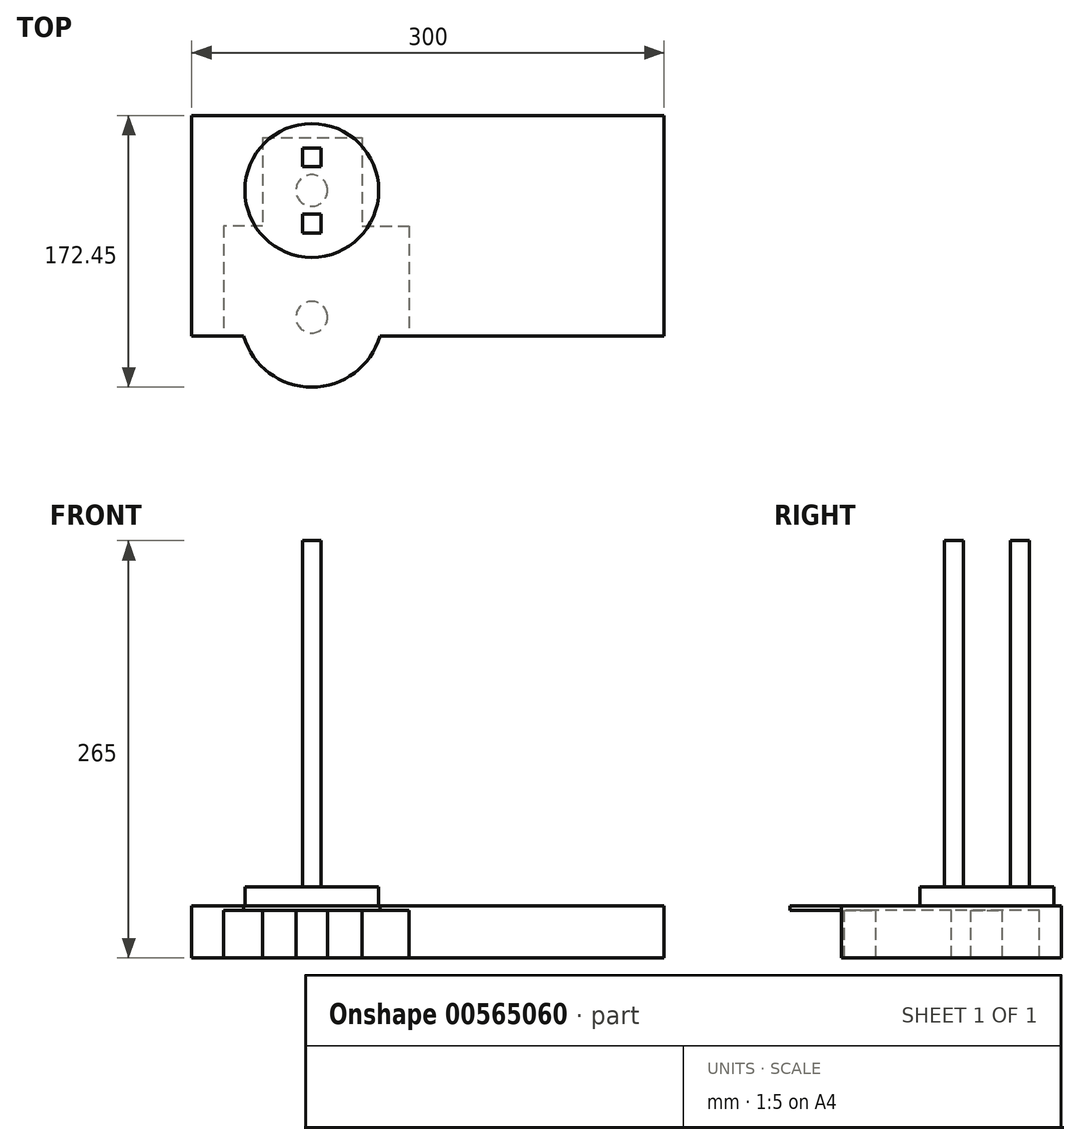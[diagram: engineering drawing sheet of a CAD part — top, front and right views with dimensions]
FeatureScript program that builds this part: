
annotation { "Feature Type Name" : "Feature", "Feature Type Description" : "" }
export const myFeature = defineFeature(function(context is Context, id is Id, definition is map)
    precondition{}
    {
        {
            var Q0;
            Q0=qCreatedBy(makeId("Top.planeOp"),FACE);
            var sketch = newSketch(context, id + "F0", { "sketchPlane" : qUnion([Q0])});
            skCircle(sketch, "E0", {"center": v(0, 0) * mm, "radius": 42.5 * mm});
            skSolve(sketch);
        }
        {
            var Q0;
            Q0=makeQuery(id+"F0.imprint","IMPRINT",FACE,{"disambiguationData":[TD([[makeQuery(id+"F0.imprint","IMPRINT",EDGE,{"derivedFrom":sQuery(id+"F0.wireOp",EDGE,"E0")}),1.0]])]});
            extrude(context, id + "F1", {"entities" : qUnion([Q0]), "depth" : 15 * mm, "offsetDistance" : 25.4 * mm});
        }
        {
            var Q0;
            Q0=qCreatedBy(makeId("Top.planeOp"),FACE);
            var sketch = newSketch(context, id + "F2", { "sketchPlane" : qUnion([Q0])});
            skLineSegment(sketch, "E1.bottom", {"start": v(-76.19, 47.5) * mm, "end": v(223.81, 47.5) * mm});
            skLineSegment(sketch, "E1.top", {"start": v(-76.19, -92.5) * mm, "end": v(-43.21, -92.5) * mm});
            skLineSegment(sketch, "E1.left", {"start": v(-76.19, 47.5) * mm, "end": v(-76.19, -92.5) * mm});
            skLineSegment(sketch, "E1.right", {"start": v(223.81, 47.5) * mm, "end": v(223.81, -92.5) * mm});
            skCircle(sketch, "E2", {"center": v(0, 0) * mm, "radius": 22.5 * mm});
            skCircle(sketch, "E3", {"center": v(0, -79.95) * mm, "radius": 45 * mm});
            skLineSegment(sketch, "E4.trimOffspring", {"start": v(43.21, -92.5) * mm, "end": v(223.81, -92.5) * mm});
            skLineSegment(sketch, "E5", {"start": v(-31.1, 33.5) * mm, "end": v(-31.1, -22.5) * mm});
            skLineSegment(sketch, "E6", {"start": v(-31.1, -22.5) * mm, "end": v(-56.1, -22.5) * mm});
            skLineSegment(sketch, "E7", {"start": v(-56.1, -22.5) * mm, "end": v(-56.1, -92.5) * mm});
            skLineSegment(sketch, "E8", {"start": v(31.9, 33.5) * mm, "end": v(31.9, -22.5) * mm});
            skLineSegment(sketch, "E9", {"start": v(31.9, -22.5) * mm, "end": v(61.9, -22.5) * mm});
            skLineSegment(sketch, "E10", {"start": v(61.9, -22.5) * mm, "end": v(61.9, -92.5) * mm});
            skLineSegment(sketch, "E11", {"start": v(-31.1, 33.5) * mm, "end": v(31.9, 33.5) * mm});
            skSolve(sketch);
        }
        {
            var Q0;
            {var subQ1=sQuery(id+"F2.wireOp",EDGE,"E1.left");Q0=makeQuery(id+"F2.imprint","IMPRINT",FACE,{"disambiguationData":[TD([[makeQuery(id+"F2.imprint","IMPRINT",EDGE,{"derivedFrom":subQ1}),1.0]])]});}
            var Q1;
            {var subQ2=sQuery(id+"F2.wireOp",EDGE,"E1.right");Q1=makeQuery(id+"F2.imprint","IMPRINT",FACE,{"disambiguationData":[TD([[makeQuery(id+"F2.imprint","IMPRINT",EDGE,{"derivedFrom":subQ2}),-1.0]])]});}
            extrude(context, id + "F3", {"entities" : qUnion([Q0, Q1]), "operationType" : NewBodyOperationType.ADD, "oppositeDirection" : true, "depth" : 30 * mm, "offsetDistance" : 25 * mm});
        }
        {
            var Q0;
            Q0 = qSketchRegion(id + "F2", true);
            extrude(context, id + "F4", {"entities" : qUnion([Q0]), "operationType" : NewBodyOperationType.ADD, "depth" : 3 * mm, "offsetDistance" : 25 * mm});
        }
        {
            var Q0;
            Q0=qCreatedBy(makeId("Top.planeOp"),FACE);
            var sketch = newSketch(context, id + "F5", { "sketchPlane" : qUnion([Q0])});
            skCircle(sketch, "E12", {"center": v(0, 0) * mm, "radius": 10 * mm});
            skSolve(sketch);
        }
        {
            var Q0;
            Q0 = qSketchRegion(id + "F5", true);
            extrude(context, id + "F6", {"entities" : qUnion([Q0]), "operationType" : NewBodyOperationType.ADD, "oppositeDirection" : true, "depth" : 30 * mm, "offsetDistance" : 25 * mm});
        }
        {
            var Q0;
            Q0 = qSketchRegion(id + "F5", true);
            extrude(context, id + "F7", {"entities" : qUnion([Q0]), "operationType" : NewBodyOperationType.ADD, "depth" : 15 * mm, "offsetDistance" : 25 * mm});
        }
        {
            var Q0;
            Q0=qCreatedBy(makeId("Top.planeOp"),FACE);
            var sketch = newSketch(context, id + "F8", { "sketchPlane" : qUnion([Q0])});
            skPoint(sketch, "E13", {"position": v(0, -80.54) * mm});
            skCircle(sketch, "E14", {"center": v(0, -80.54) * mm, "radius": 10 * mm});
            skSolve(sketch);
        }
        {
            var Q0;
            Q0 = qSketchRegion(id + "F8", true);
            extrude(context, id + "F9", {"entities" : qUnion([Q0]), "operationType" : NewBodyOperationType.ADD, "oppositeDirection" : true, "depth" : 30 * mm, "offsetDistance" : 25 * mm});
        }
        {
            var Q0;
            Q0=makeQuery(id+"F1.opExtrude","CAP_FACE",FACE,{"disambiguationData":[OSD([sQuery(id+"F0.wireOp",EDGE,"E0")])],"isStart":false});
            var sketch = newSketch(context, id + "F10", { "sketchPlane" : qUnion([Q0])});
            skLineSegment(sketch, "E15.top", {"start": v(-6, 15) * mm, "end": v(6, 15) * mm});
            skLineSegment(sketch, "E16.bottom", {"start": v(-6, -15) * mm, "end": v(6, -15) * mm});
            skLineSegment(sketch, "E16.top", {"start": v(-6, -27) * mm, "end": v(6, -27) * mm});
            skLineSegment(sketch, "E16.left", {"start": v(-6, -15) * mm, "end": v(-6, -27) * mm});
            skLineSegment(sketch, "E16.right", {"start": v(6, -15) * mm, "end": v(6, -27) * mm});
            skLineSegment(sketch, "E17", {"start": v(0, 0) * mm, "end": v(0, 15) * mm});
            skPoint(sketch, "E17.endSnap0", {"position": v(0, 15) * mm});
            skLineSegment(sketch, "E18", {"start": v(0, 15) * mm, "end": v(0, 0) * mm});
            skLineSegment(sketch, "E19", {"start": v(0, 0) * mm, "end": v(0, -15) * mm});
            skPoint(sketch, "E19.endSnap0", {"position": v(0, -15) * mm});
            skLineSegment(sketch, "E20", {"start": v(-6, 15) * mm, "end": v(-6, 27) * mm});
            skLineSegment(sketch, "E21", {"start": v(-6, 27) * mm, "end": v(6, 27) * mm});
            skLineSegment(sketch, "E22", {"start": v(6, 27) * mm, "end": v(6, 15) * mm});
            skSolve(sketch);
        }
        {
            var Q0;
            {var subQ0=sQuery(id+"F10.wireOp",EDGE,"E20");Q0=makeQuery(id+"F10.imprint","IMPRINT",FACE,{"disambiguationData":[TD([[makeQuery(id+"F10.imprint","IMPRINT",EDGE,{"derivedFrom":subQ0}),-1.0]])]});}
            var Q1;
            Q1=makeQuery(id+"F10.imprint","IMPRINT",FACE,{"disambiguationData":[TD([[makeQuery(id+"F10.imprint","IMPRINT",EDGE,{"derivedFrom":sQuery(id+"F10.wireOp",EDGE,"E16.top")}),1.0]])]});
            extrude(context, id + "F11", {"entities" : qUnion([Q0, Q1]), "operationType" : NewBodyOperationType.ADD, "depth" : 220 * mm, "offsetDistance" : 25 * mm});
        }
    });
